# Revit family: Washfountain_Lavatory-Bradley_Corp-WF2704-Type_A_Drain
name_source: partatom
category: Plumbing Fixtures
revit_build: Autodesk Revit MEP 2012 (Build: 20110309_2315(x64)
units: mm (PartAtom-declared; Revit-internal decimal feet)

## types (1)
- Washfountain_Lavatory-Bradley_Corp-WF2704-Type_A_Drain
    ADA Compliant = Yes
    Assembly Code = D2010300
    Buy American Act = No
    CWFU = 0
    Cold Lavatory Inlet Primary = 1"
    Cold Lavatory Inlet Primary Radius = 1/2"
    Cold Lavatory Inlet Secondary = 1"
    Cold Lavatory Inlet Secondary Radius = 1/2"
    Description = Washfountain, 54" Semi Circular with 9" Deep Bowl
    Drain Primary = 2"
    Drain Primary Radius = 1"
    Drain Secondary = 2"
    Drain Secondary Radius = 1"
    Flow Rate = 3.0 gal/min
    Frequency = 50 Hz
    HWFU = 0
    Hot Lavatory Inlet Primary = 1"
    Hot Lavatory Inlet Primary Radius = 1/2"
    Hot Lavatory Inlet Secondary = 1"
    Hot Lavatory Inlet Secondary Radius = 1/2"
    Manufacturer = Bradley Corp
    MasterFormat Number = 22 42 16
    MasterFormat Title = Commercial Lavatories and Sinks
    Model = WF2704
    OmniClass Table 21 Number = 21-04 20 10 60
    OmniClass Table 21 Title = Plumbing Fixtures
    OmniClass Table 23 Number = 23-31 13 00
    OmniClass Table 23 Title = Sinks/Lavatories
    Operating Water Pressure Range = 20 - 80 PSI
    Pedestal Height = 19 "
    Pedestal Material = Metal - Bradley Corp - Stainless Steel - Satin
    Product Tech Data URL - English = http://bradleycorp.com
    Rim Height = 28 "
    Sensor Module Height = 40.875 "
    Specifications URL = http://www.bradleycorp.com
    Spray Head Height = 37.375 "
    URL = http://www.bradleycorp.com
    Vent = 1 1/2"
    Vent Radius = 3/4"
    Version = 2.0
    Voltage = 24 V
    WFU = 0
    Width = 54 "

## geometry (parser evidence)
native form markers: Blend x12, Sweep x2
no freeform markers — native parametric forms only
